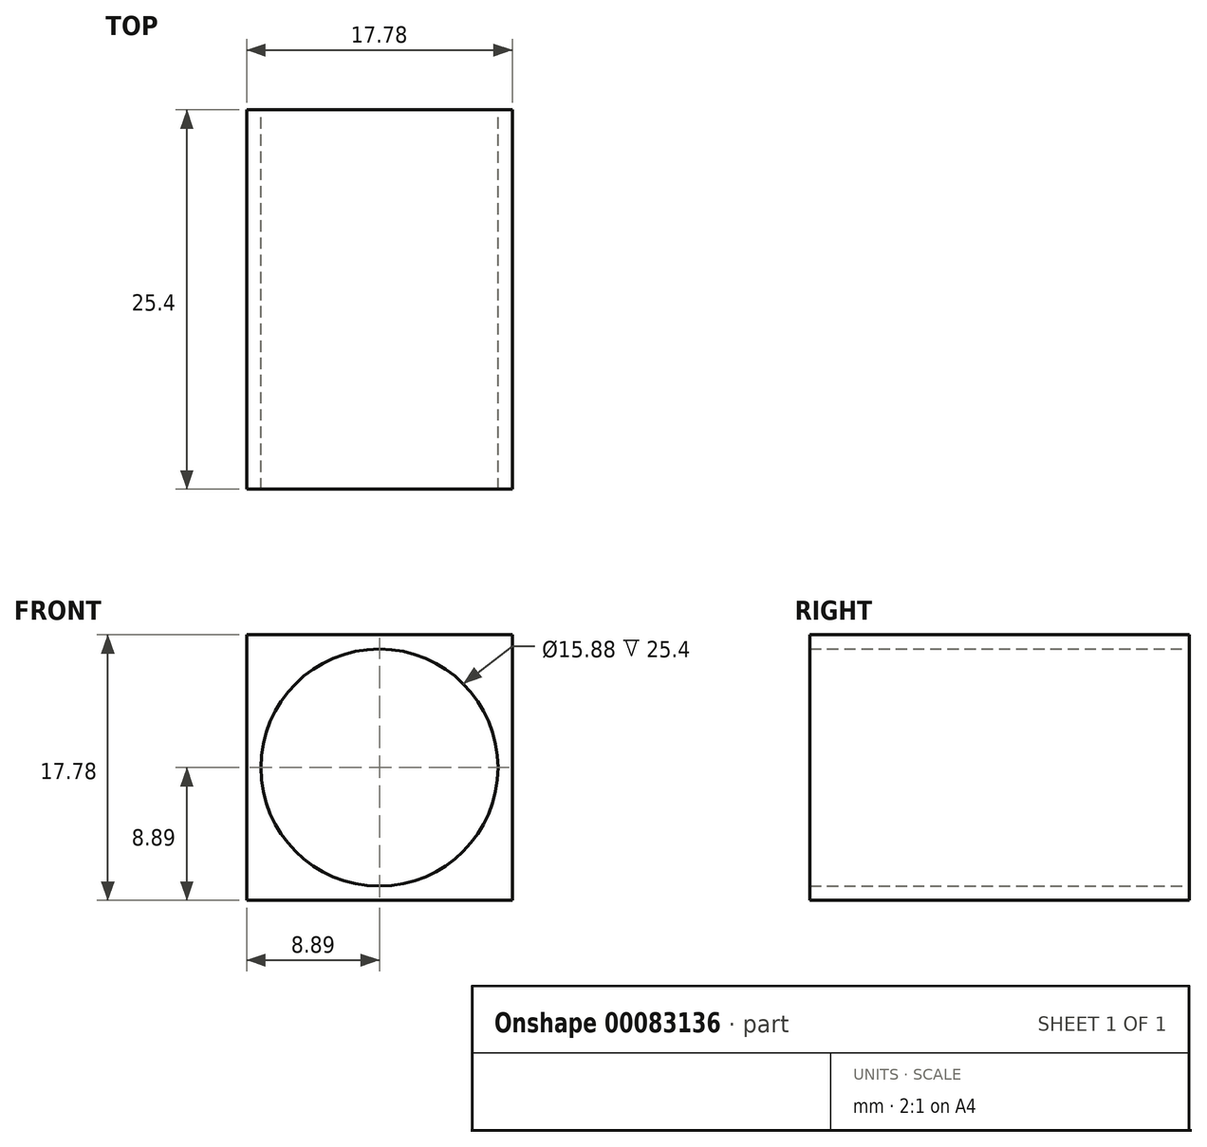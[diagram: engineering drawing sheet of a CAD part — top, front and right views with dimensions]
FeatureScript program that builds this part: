
annotation { "Feature Type Name" : "Feature", "Feature Type Description" : "" }
export const myFeature = defineFeature(function(context is Context, id is Id, definition is map)
    precondition{}
    {
        {
            var Q0;
            Q0=qCreatedBy(makeId("Front.planeOp"),FACE);
            var sketch = newSketch(context, id + "F0", { "sketchPlane" : qUnion([Q0])});
            skLineSegment(sketch, "E0.bottom", {"start": v(0, 0) * mm, "end": v(17.78, 0) * mm});
            skLineSegment(sketch, "E0.top", {"start": v(0, 17.78) * mm, "end": v(17.78, 17.78) * mm});
            skLineSegment(sketch, "E0.left", {"start": v(0, 0) * mm, "end": v(0, 17.78) * mm});
            skLineSegment(sketch, "E0.right", {"start": v(17.78, 0) * mm, "end": v(17.78, 17.78) * mm});
            skPoint(sketch, "E1", {"position": v(8.89, 8.9) * mm});
            skCircle(sketch, "E2", {"center": v(8.89, 8.9) * mm, "radius": 7.94 * mm});
            skSolve(sketch);
        }
        {
            var Q0;
            Q0=makeQuery(id+"F0.imprint","IMPRINT",FACE,{"disambiguationData":[TD([[makeQuery(id+"F0.imprint","IMPRINT",EDGE,{"derivedFrom":sQuery(id+"F0.wireOp",EDGE,"E0.bottom")}),1.0]])]});
            extrude(context, id + "F1", {"entities" : qUnion([Q0]), "depth" : 25.4 * mm});
        }
    });
